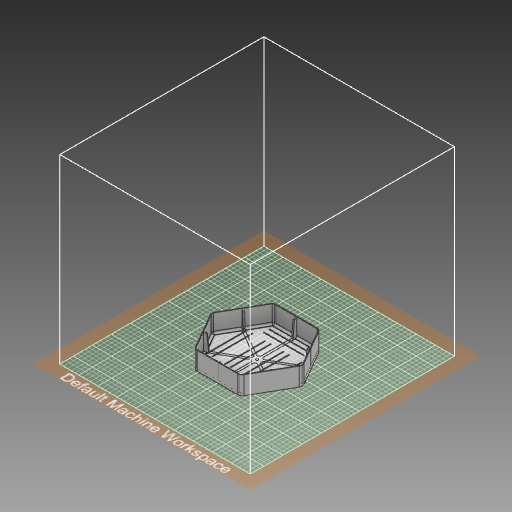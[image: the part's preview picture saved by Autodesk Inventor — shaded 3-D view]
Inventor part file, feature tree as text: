
AUTODESK INVENTOR PART (.ipt)
format: ipt  version: 2019 (Build 230136000, 136)  size: 959,488 bytes
history: native  units: mm
features: projected_geometry x23, sketch x9, extrude x5, plane x3, fillet x3, other x3, shell x1, pattern_circular x1
ambient origin geometry x8: Origin, YZ Plane, XZ Plane, XY Plane, X Axis, Y Axis, Z Axis, Center Point
bodies: Solid1 (feature_tree)
feature tree (48):
  extrude  "Extrusion1"  Depth=40.0mm TaperAngle=0.0deg
  shell  "Shell1"  Thickness=1.5mm
  extrude  "Extrusion9"  Depth=10.0mm
  plane  "Work Plane1"
  plane  "Work Plane2"
  plane  "Work Plane3"
  sketch  "Sketch12"  dims[d55=5.0mm]
  extrude  "Extrusion5"  Depth=5.0mm
  extrude  "Extrusion6"  TaperAngle=60.0deg  [1 undecoded]
  extrude  "Extrusion8"  TaperAngle=90.0deg  [1 undecoded]
  pattern_circular  "Circular Pattern1"  [2 undecoded]
  fillet  "Fillet1"  Radius=8.0mm
  fillet  "Fillet2"  Radius=36.0mm
  fillet  "Fillet4"  Radius=60.0mm
  sketch  "Sketch5"  dims[d12=1.0mm d37=5.0mm]
  sketch  "Sketch6"  dims[d44=10.0mm d45=60.0deg]
  sketch  "Sketch7"  dims[d46=90.0deg d47=90.0deg]
  other  "Work Axis4"
  other  "Work Axis5"
  other  "Work Axis6"
  sketch  "Sketch13"  dims[d56=2.0mm d57=3.0mm d58=8.0mm d59=36.0mm d60=0.0mm d70=60.0mm d72=360.0deg d74=60.0mm d75=360.0deg d77=3.0mm d78=30.0mm d79=20.0mm d80=0.0mm d138=11.0mm d139=87.0mm d140=40.0mm d142=40.5mm d143=10.0mm d145=10.0mm d147=130.0mm d149=0.5mm d150=0.0mm d151=1.0mm d152=1.0mm d153=1.0mm d154=1.0mm d155=1.0mm d156=1.0mm]
  sketch  "Sketch1"  dims[d0=175.0mm d2=40.0mm d3=0.0mm d4=1.5mm]
  sketch  "Sketch4"  dims[d10=4.0mm d11=10.0mm]
  projected_geometry  "Projected Loop3"
  sketch  "Sketch8"  dims[d52=5.5mm]
  projected_geometry  "Projected Loop4"
  sketch  "Sketch9"  dims[d53=0.01mm d54=0.0mm]
  projected_geometry  "Projected Loop5"
  projected_geometry  "Projected Loop6"
  projected_geometry  "Projected Loop7"
  projected_geometry  "Projected Loop8"
  projected_geometry  "Projected Loop9"
  projected_geometry  "Projected Loop10"
  projected_geometry  "Projected Loop11"
  projected_geometry  "Projected Loop12"
  projected_geometry  "Projected Loop13"
  projected_geometry  "Projected Loop14"
  projected_geometry  "Projected Loop15"
  projected_geometry  "Projected Loop16"
  projected_geometry  "Projected Loop17"
  projected_geometry  "Projected Loop18"
  projected_geometry  "Projected Loop19"
  projected_geometry  "Projected Loop20"
  projected_geometry  "Projected Loop21"
  projected_geometry  "Projected Loop22"
  projected_geometry  "Projected Loop23"
  projected_geometry  "Projected Loop24"
  projected_geometry  "Projected Loop25"
note: 4 required parameter values undecoded (feature->parameter linkage not recoverable at this tier; creation-order binding heuristic only, values carry confidence <= 0.55)
